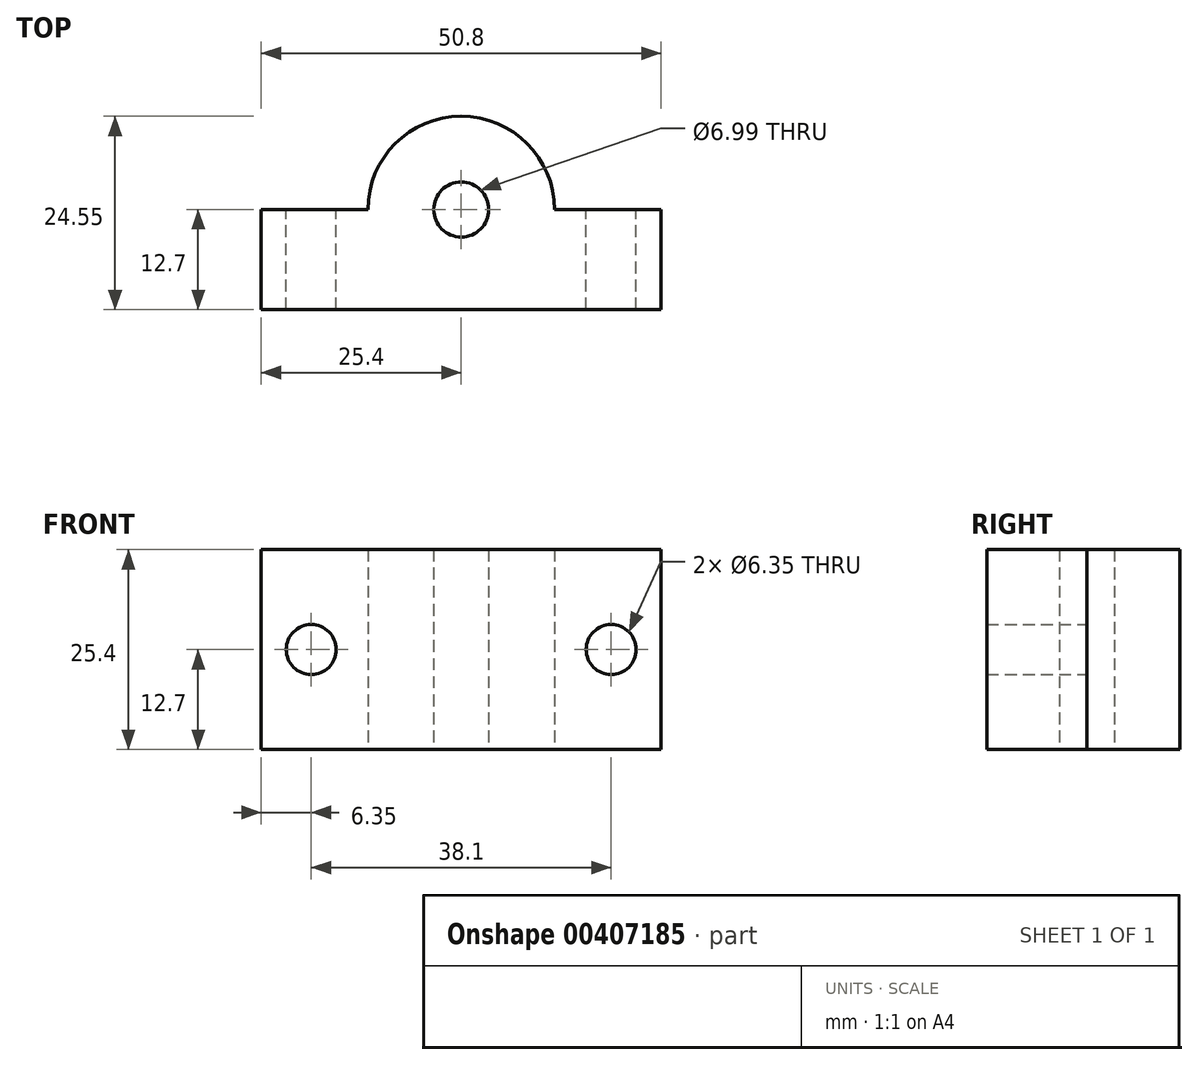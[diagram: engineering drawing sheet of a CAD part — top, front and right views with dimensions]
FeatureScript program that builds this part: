
annotation { "Feature Type Name" : "Feature", "Feature Type Description" : "" }
export const myFeature = defineFeature(function(context is Context, id is Id, definition is map)
    precondition{}
    {
        {
            var Q0;
            Q0=qCreatedBy(makeId("Top.planeOp"),FACE);
            var sketch = newSketch(context, id + "F0", { "sketchPlane" : qUnion([Q0])});
            skCircle(sketch, "E0", {"center": v(0, 0) * mm, "radius": 3.5 * mm});
            skArc(sketch, "E1", {"start": v(11.85, 0) * mm, "mid": v(0, 11.85) * mm, "end": v(-11.85, 0) * mm});
            skLineSegment(sketch, "E2.bottom", {"start": v(-25.4, 0) * mm, "end": v(-11.85, 0) * mm});
            skLineSegment(sketch, "E2.top", {"start": v(-25.4, -12.7) * mm, "end": v(25.4, -12.7) * mm});
            skLineSegment(sketch, "E2.left", {"start": v(-25.4, 0) * mm, "end": v(-25.4, -12.7) * mm});
            skLineSegment(sketch, "E2.right", {"start": v(25.4, 0) * mm, "end": v(25.4, -12.7) * mm});
            skLineSegment(sketch, "E3.trimOffspring", {"start": v(11.85, 0) * mm, "end": v(25.4, 0) * mm});
            skLineSegment(sketch, "E4.trimOffspring", {"start": v(-3.5, 0) * mm, "end": v(3.5, 0) * mm});
            skSolve(sketch);
        }
        {
            var Q0;
            Q0=makeQuery(id+"F0.imprint","IMPRINT",FACE,{"disambiguationData":[TD([[makeQuery(id+"F0.imprint","IMPRINT",EDGE,{"derivedFrom":sQuery(id+"F0.wireOp",EDGE,"E1")}),1.0]])]});
            extrude(context, id + "F1", {"entities" : qUnion([Q0]), "depth" : 25.4 * mm});
        }
        {
            var Q0;
            Q0=makeQuery(id+"F1.opExtrude","SWEPT_FACE",FACE,{"disambiguationData":[OSD([sQuery(id+"F0.wireOp",EDGE,"E3.trimOffspring")])]});
            var sketch = newSketch(context, id + "F2", { "sketchPlane" : qUnion([Q0])});
            skCircle(sketch, "E5", {"center": v(-19.05, 12.7) * mm, "radius": 3.18 * mm});
            skPoint(sketch, "E5.centerSnap0", {"position": v(-11.85, 12.7) * mm});
            skCircle(sketch, "E6", {"center": v(19.05, 12.7) * mm, "radius": 3.18 * mm});
            skSolve(sketch);
        }
        {
            var Q0;
            Q0=makeQuery(id+"F2.imprint","IMPRINT",FACE,{"disambiguationData":[TD([[makeQuery(id+"F2.imprint","IMPRINT",EDGE,{"derivedFrom":sQuery(id+"F2.wireOp",EDGE,"E6")}),1.0]])]});
            var Q1;
            Q1=makeQuery(id+"F2.imprint","IMPRINT",FACE,{"disambiguationData":[TD([[makeQuery(id+"F2.imprint","IMPRINT",EDGE,{"derivedFrom":sQuery(id+"F2.wireOp",EDGE,"E5")}),1.0]])]});
            extrude(context, id + "F3", {"entities" : qUnion([Q0, Q1]), "operationType" : NewBodyOperationType.REMOVE, "oppositeDirection" : true, "depth" : 25.4 * mm});
        }
    });
